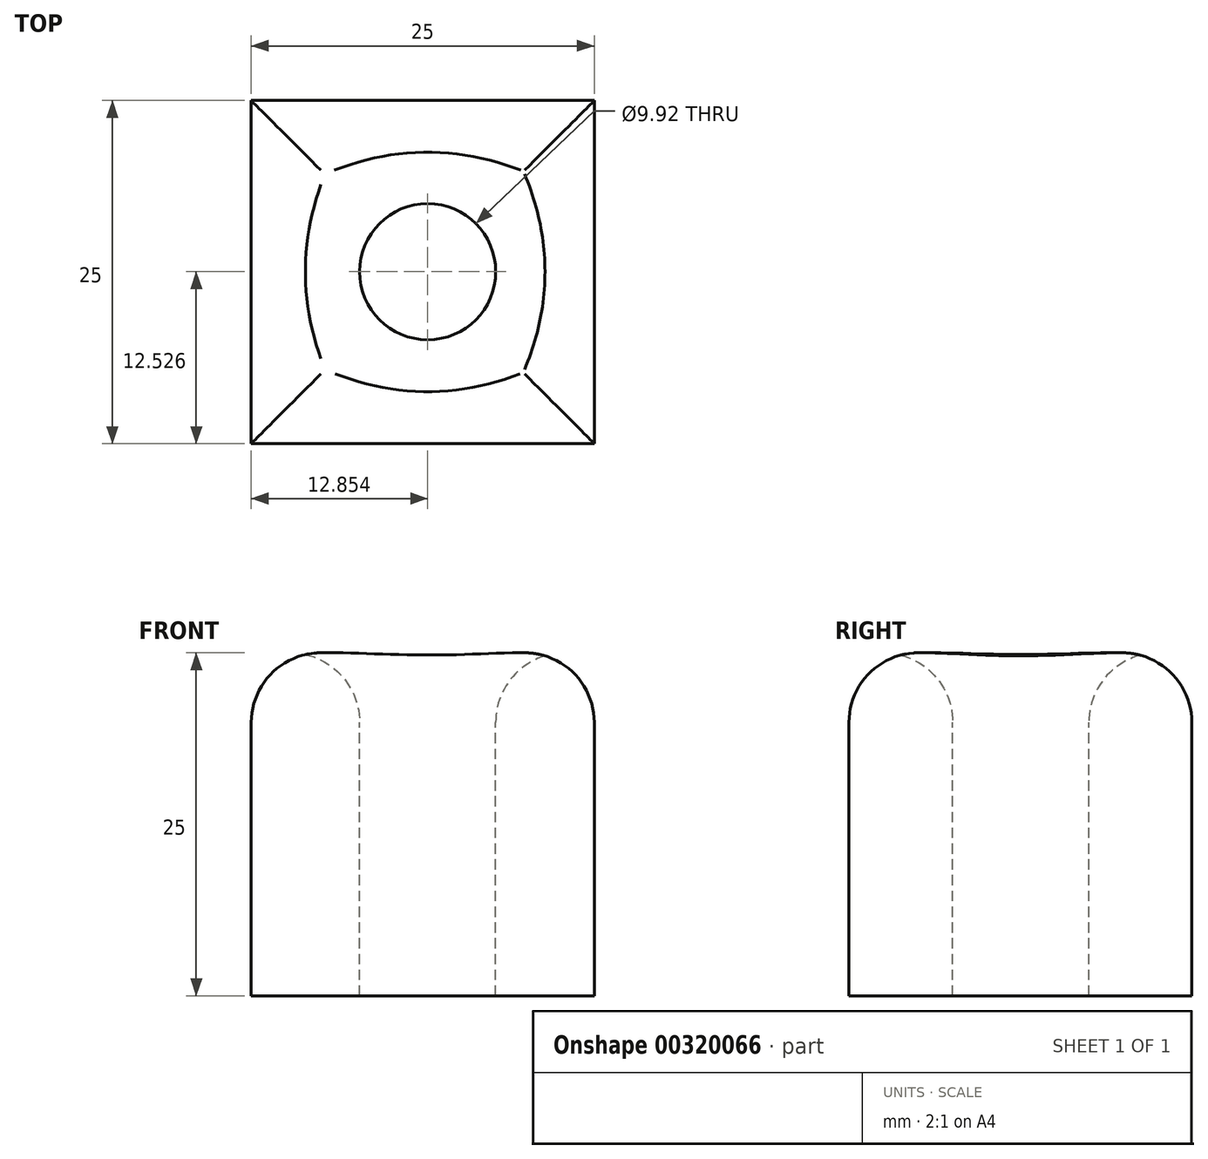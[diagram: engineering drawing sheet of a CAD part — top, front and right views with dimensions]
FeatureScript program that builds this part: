
annotation { "Feature Type Name" : "Feature", "Feature Type Description" : "" }
export const myFeature = defineFeature(function(context is Context, id is Id, definition is map)
    precondition{}
    {
        {
            var Q0;
            Q0=qCreatedBy(makeId("Top.planeOp"),FACE);
            var sketch = newSketch(context, id + "F0", { "sketchPlane" : qUnion([Q0])});
            skLineSegment(sketch, "E0.bottom", {"start": v(0, 0) * mm, "end": v(-25, 0) * mm});
            skLineSegment(sketch, "E0.top", {"start": v(0, -25) * mm, "end": v(-25, -25) * mm});
            skLineSegment(sketch, "E0.left", {"start": v(0, 0) * mm, "end": v(0, -25) * mm});
            skLineSegment(sketch, "E0.right", {"start": v(-25, 0) * mm, "end": v(-25, -25) * mm});
            skSolve(sketch);
        }
        {
            var Q0;
            Q0 = qSketchRegion(id + "F0", true);
            extrude(context, id + "F1", {"entities" : qUnion([Q0]), "depth" : 25 * mm});
        }
        {
            var Q0;
            Q0=makeQuery(id+"F1.opExtrude","CAP_FACE",FACE,{"disambiguationData":[OSD([sQuery(id+"F0.wireOp",EDGE,"E0.bottom"),sQuery(id+"F0.wireOp",EDGE,"E0.top"),sQuery(id+"F0.wireOp",EDGE,"E0.left"),sQuery(id+"F0.wireOp",EDGE,"E0.right")])],"isStart":false});
            var sketch = newSketch(context, id + "F2", { "sketchPlane" : qUnion([Q0])});
            skCircle(sketch, "E1", {"center": v(-12.15, -12.47) * mm, "radius": 4.96 * mm});
            skSolve(sketch);
        }
        {
            var Q0;
            Q0 = qSketchRegion(id + "F2", true);
            extrude(context, id + "F3", {"entities" : qUnion([Q0]), "operationType" : NewBodyOperationType.REMOVE, "oppositeDirection" : true, "depth" : 25.4 * mm});
        }
        {
            var Q0;
            Q0=makeQuery(id+"F1.opExtrude","CAP_FACE",FACE,{"disambiguationData":[OSD([sQuery(id+"F0.wireOp",EDGE,"E0.bottom"),sQuery(id+"F0.wireOp",EDGE,"E0.top"),sQuery(id+"F0.wireOp",EDGE,"E0.left"),sQuery(id+"F0.wireOp",EDGE,"E0.right")])],"isStart":false});
            fillet(context, id + "F4", {"entities" : qUnion([Q0]), "radius" : 5.08 * mm, "tangentPropagation" : true, "allowEdgeOverflow" : false});
        }
    });
